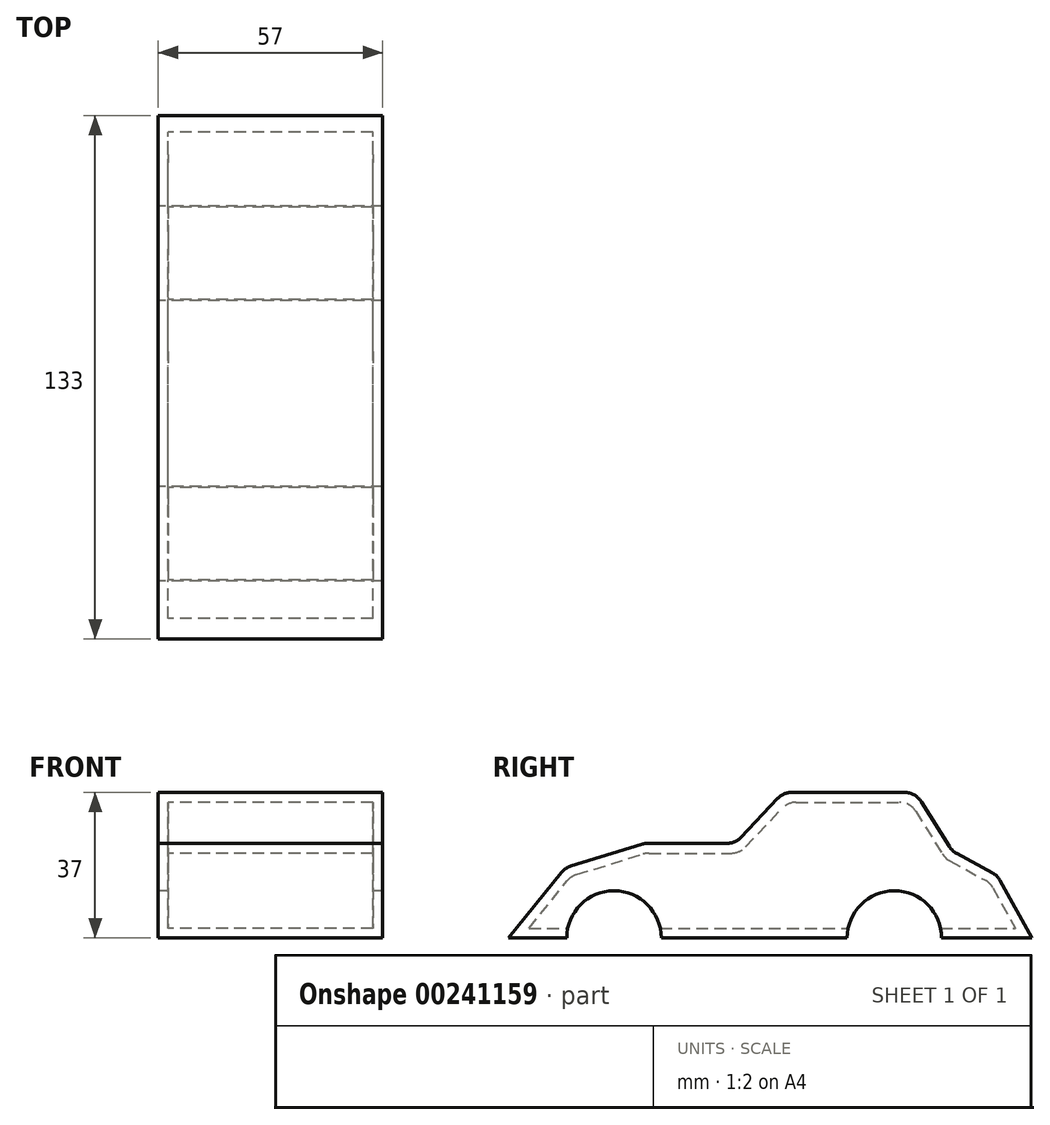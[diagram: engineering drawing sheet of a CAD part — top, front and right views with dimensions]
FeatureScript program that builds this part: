
annotation { "Feature Type Name" : "Feature", "Feature Type Description" : "" }
export const myFeature = defineFeature(function(context is Context, id is Id, definition is map)
    precondition{}
    {
        {
            var Q0;
            Q0=qCreatedBy(makeId("Right.planeOp"),FACE);
            var sketch = newSketch(context, id + "F0", { "sketchPlane" : qUnion([Q0])});
            skLineSegment(sketch, "E0.bottom", {"start": v(-62.27, 0) * mm, "end": v(70.73, 0) * mm});
            skLineSegment(sketch, "E0.top", {"start": v(-62.27, 37) * mm, "end": v(70.73, 37) * mm});
            skLineSegment(sketch, "E0.left", {"start": v(-62.27, 0) * mm, "end": v(-62.27, 37) * mm});
            skLineSegment(sketch, "E0.right", {"start": v(70.73, 0) * mm, "end": v(70.73, 37) * mm});
            skCircle(sketch, "E1", {"center": v(-35.5, 0) * mm, "radius": 12 * mm});
            skCircle(sketch, "E2", {"center": v(35.73, 0) * mm, "radius": 12 * mm});
            skLineSegment(sketch, "E3", {"start": v(-62.27, 0) * mm, "end": v(-47.9, 17.84) * mm});
            skLineSegment(sketch, "E4", {"start": v(-47.9, 17.84) * mm, "end": v(-27.74, 24.05) * mm});
            skLineSegment(sketch, "E5", {"start": v(-27.74, 24.05) * mm, "end": v(-4.66, 24.05) * mm});
            skLineSegment(sketch, "E6", {"start": v(-4.66, 24.05) * mm, "end": v(7.56, 37) * mm});
            skLineSegment(sketch, "E7", {"start": v(7.56, 37) * mm, "end": v(41.12, 37) * mm});
            skLineSegment(sketch, "E8", {"start": v(41.12, 37) * mm, "end": v(50.43, 22.11) * mm});
            skLineSegment(sketch, "E9", {"start": v(50.43, 22.11) * mm, "end": v(61.88, 15.9) * mm});
            skLineSegment(sketch, "E10", {"start": v(61.88, 15.9) * mm, "end": v(70.73, 0) * mm});
            skLineSegment(sketch, "E11", {"start": v(35.73, 0) * mm, "end": v(70.73, 0) * mm});
            skSolve(sketch);
        }
        {
            var Q0;
            {var subQ5=sQuery(id+"F0.wireOp",EDGE,"E3");Q0=makeQuery(id+"F0.imprint","IMPRINT",FACE,{"disambiguationData":[TD([[makeQuery(id+"F0.imprint","IMPRINT",EDGE,{"derivedFrom":subQ5}),-1.0]])]});}
            extrude(context, id + "F1", {"entities" : qUnion([Q0]), "depth" : 57 * mm});
        }
        {
            var Q0;
            {var subQ0=sQuery(id+"F0.wireOp",EDGE,"E0.bottom");Q0=makeQuery(id+"F1.opExtrude","SWEPT_FACE",FACE,{"disambiguationData":[OSD([subQ0]),TDD([makeQuery(id+"F0.imprint","IMPRINT",EDGE,{"disambiguationData":[TD([[makeQuery(id+"F0.imprint","INTERSECT",VERTEX,{"disambiguationData":[OD(1.0)],"derivedFrom":[subQ0,sQuery(id+"F0.wireOp",EDGE,"E1")]}),-1.0]])],"derivedFrom":subQ0})])]});}
            var Q1;
            Q1=makeQuery(id+"F1.opExtrude","SWEPT_FACE",FACE,{"disambiguationData":[OSD([sQuery(id+"F0.wireOp",EDGE,"E1")])]});
            var Q2;
            Q2=makeQuery(id+"F1.opExtrude","SWEPT_FACE",FACE,{"disambiguationData":[OSD([sQuery(id+"F0.wireOp",EDGE,"E2")])]});
            var Q3;
            Q3=makeQuery(id+"F1.opExtrude","SWEPT_FACE",FACE,{"disambiguationData":[OSD([sQuery(id+"F0.wireOp",EDGE,"E11")])]});
            var Q4;
            {var subQ0=sQuery(id+"F0.wireOp",EDGE,"E0.bottom");Q4=makeQuery(id+"F1.opExtrude","SWEPT_FACE",FACE,{"disambiguationData":[OSD([subQ0]),TDD([makeQuery(id+"F0.imprint","IMPRINT",EDGE,{"disambiguationData":[TD([[makeQuery(id+"F0.imprint","INTERSECT",VERTEX,{"disambiguationData":[OD(0.0)],"derivedFrom":[subQ0,sQuery(id+"F0.wireOp",EDGE,"E1")]}),1.0]])],"derivedFrom":subQ0})])]});}
            shell(context, id + "F2", {"entities" : qUnion([Q0, Q1, Q2, Q3, Q4]), "thickness" : 2.5 * mm});
        }
        {
            var Q0;
            Q0=makeQuery(id+"F1.opExtrude","SWEPT_EDGE",EDGE,{"disambiguationData":[OSD([sQuery(id+"F0.wireOp",EDGE,"E3"),sQuery(id+"F0.wireOp",EDGE,"E4")])]});
            var Q1;
            Q1=makeQuery(id+"F1.opExtrude","SWEPT_EDGE",EDGE,{"disambiguationData":[OSD([sQuery(id+"F0.wireOp",EDGE,"E4"),sQuery(id+"F0.wireOp",EDGE,"E5")])]});
            var Q2;
            Q2=makeQuery(id+"F1.opExtrude","SWEPT_EDGE",EDGE,{"disambiguationData":[OSD([sQuery(id+"F0.wireOp",EDGE,"E5"),sQuery(id+"F0.wireOp",EDGE,"E6")])]});
            var Q3;
            Q3=makeQuery(id+"F1.opExtrude","SWEPT_EDGE",EDGE,{"disambiguationData":[OSD([sQuery(id+"F0.wireOp",EDGE,"E0.top"),sQuery(id+"F0.wireOp",EDGE,"E6"),sQuery(id+"F0.wireOp",EDGE,"E7")])]});
            var Q4;
            Q4=makeQuery(id+"F1.opExtrude","SWEPT_EDGE",EDGE,{"disambiguationData":[OSD([sQuery(id+"F0.wireOp",EDGE,"E0.top"),sQuery(id+"F0.wireOp",EDGE,"E7"),sQuery(id+"F0.wireOp",EDGE,"E8")])]});
            var Q5;
            Q5=makeQuery(id+"F1.opExtrude","SWEPT_EDGE",EDGE,{"disambiguationData":[OSD([sQuery(id+"F0.wireOp",EDGE,"E8"),sQuery(id+"F0.wireOp",EDGE,"E9")])]});
            var Q6;
            Q6=makeQuery(id+"F1.opExtrude","SWEPT_EDGE",EDGE,{"disambiguationData":[OSD([sQuery(id+"F0.wireOp",EDGE,"E9"),sQuery(id+"F0.wireOp",EDGE,"E10")])]});
            fillet(context, id + "F3", {"entities" : qUnion([Q0, Q1, Q2, Q3, Q4, Q5, Q6]), "radius" : 5 * mm, "tangentPropagation" : true, "allowEdgeOverflow" : false});
        }
        {
            var Q0;
            Q0=makeQuery(id+"F2.opShell","OFFSET_EDGE",EDGE,{"disambiguationData":[OSD([sQuery(id+"F0.wireOp",EDGE,"E3"),sQuery(id+"F0.wireOp",EDGE,"E4")])]});
            var Q1;
            Q1=makeQuery(id+"F2.opShell","OFFSET_EDGE",EDGE,{"disambiguationData":[OSD([sQuery(id+"F0.wireOp",EDGE,"E4"),sQuery(id+"F0.wireOp",EDGE,"E5")])]});
            var Q2;
            Q2=makeQuery(id+"F2.opShell","OFFSET_EDGE",EDGE,{"disambiguationData":[OSD([sQuery(id+"F0.wireOp",EDGE,"E5"),sQuery(id+"F0.wireOp",EDGE,"E6")])]});
            var Q3;
            Q3=makeQuery(id+"F2.opShell","OFFSET_EDGE",EDGE,{"disambiguationData":[OSD([sQuery(id+"F0.wireOp",EDGE,"E0.top"),sQuery(id+"F0.wireOp",EDGE,"E6"),sQuery(id+"F0.wireOp",EDGE,"E7")])]});
            var Q4;
            Q4=makeQuery(id+"F2.opShell","OFFSET_EDGE",EDGE,{"disambiguationData":[OSD([sQuery(id+"F0.wireOp",EDGE,"E0.top"),sQuery(id+"F0.wireOp",EDGE,"E7"),sQuery(id+"F0.wireOp",EDGE,"E8")])]});
            var Q5;
            Q5=makeQuery(id+"F2.opShell","OFFSET_EDGE",EDGE,{"disambiguationData":[OSD([sQuery(id+"F0.wireOp",EDGE,"E8"),sQuery(id+"F0.wireOp",EDGE,"E9")])]});
            var Q6;
            Q6=makeQuery(id+"F2.opShell","OFFSET_EDGE",EDGE,{"disambiguationData":[OSD([sQuery(id+"F0.wireOp",EDGE,"E9"),sQuery(id+"F0.wireOp",EDGE,"E10")])]});
            fillet(context, id + "F4", {"entities" : qUnion([Q0, Q1, Q2, Q3, Q4, Q5, Q6]), "radius" : 5 * mm, "tangentPropagation" : true, "allowEdgeOverflow" : false});
        }
    });
